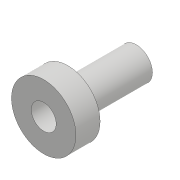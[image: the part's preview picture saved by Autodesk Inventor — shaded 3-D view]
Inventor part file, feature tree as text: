
AUTODESK INVENTOR PART (.ipt)
format: ipt  version: 2018 (Build 220112000, 112)  size: 91,648 bytes
history: native  units: mm
features: sketch x3, extrude x2, hole x1
ambient origin geometry x8: Origin, YZ Plane, XZ Plane, XY Plane, X Axis, Y Axis, Z Axis, Center Point
bodies: Solid1 (feature_tree)
feature tree (6):
  extrude  "Extrusion1"  Depth=3.0mm TaperAngle=0.0deg
  extrude  "Extrusion2"  Depth=8.5mm TaperAngle=0.0deg
  hole  "Hole1"  [1 undecoded]
  sketch  "Sketch1"  dims[d0=8.0mm d1=3.0mm d2=0.0mm]
  sketch  "Sketch2"  dims[d3=4.0mm d4=8.5mm d5=0.0mm]
  sketch  "Sketch3"  dims[d6=3.1mm d7=6.0mm d8=6.3mm d9=2.0mm d10=90.0deg d11=8.0mm d12=20.594885mm]
note: 1 required parameter value undecoded (feature->parameter linkage not recoverable at this tier; creation-order binding heuristic only, values carry confidence <= 0.55)
